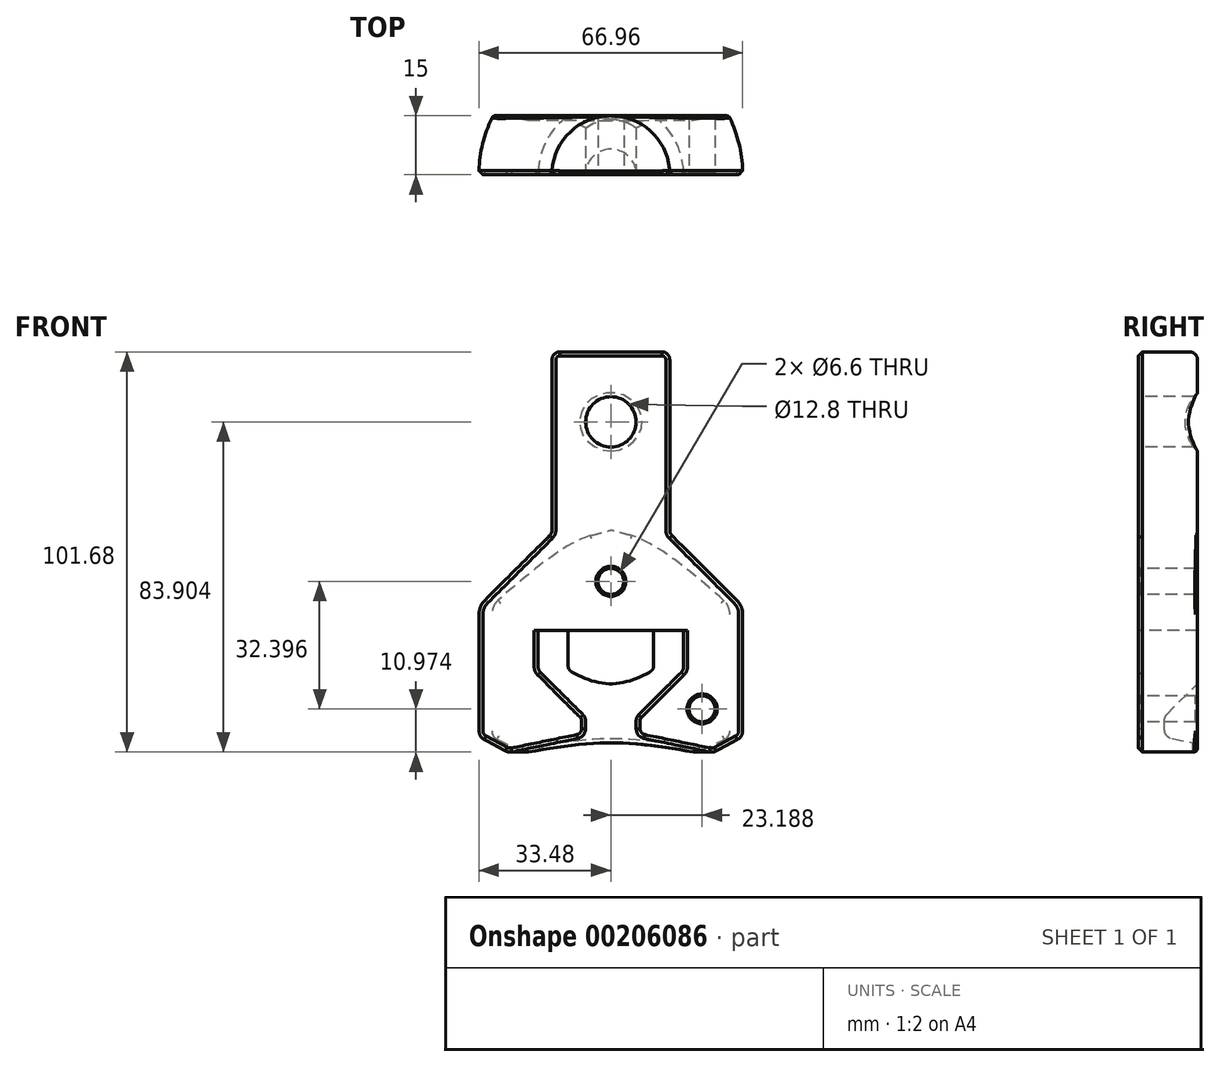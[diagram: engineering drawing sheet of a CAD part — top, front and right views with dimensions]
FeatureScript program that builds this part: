
annotation { "Feature Type Name" : "Feature", "Feature Type Description" : "" }
export const myFeature = defineFeature(function(context is Context, id is Id, definition is map)
    precondition{}
    {
        {
            var Q0;
            Q0=qCreatedBy(makeId("Front.planeOp"),FACE);
            var sketch = newSketch(context, id + "F0", { "sketchPlane" : qUnion([Q0])});
            skLineSegment(sketch, "E0", {"start": v(6.5, 0) * mm, "end": v(18.5, 12) * mm});
            skLineSegment(sketch, "E1", {"start": v(18.5, 12) * mm, "end": v(18.5, 22) * mm});
            skLineSegment(sketch, "E2", {"start": v(18.5, 22) * mm, "end": v(0, 22) * mm});
            skLineSegment(sketch, "E3", {"start": v(6.5, 0) * mm, "end": v(33.5, 0) * mm});
            skLineSegment(sketch, "E4", {"start": v(33.5, 0) * mm, "end": v(33.5, 28.21) * mm});
            skLineSegment(sketch, "E5", {"start": v(15, 92.81) * mm, "end": v(0, 92.81) * mm});
            skLineSegment(sketch, "E6", {"start": v(0, 92.81) * mm, "end": v(0, 22) * mm});
            skCircle(sketch, "E7", {"center": v(0, 75.03) * mm, "radius": 6.35 * mm});
            skPoint(sketch, "E8", {"position": v(0, 81.38) * mm});
            skLineSegment(sketch, "E9.bottom", {"start": v(18.5, 22) * mm, "end": v(-18.5, 22) * mm});
            skLineSegment(sketch, "E9.top", {"start": v(18.5, 0) * mm, "end": v(-18.5, 0) * mm});
            skLineSegment(sketch, "E9.left", {"start": v(18.5, 22) * mm, "end": v(18.5, 0) * mm});
            skLineSegment(sketch, "E9.right", {"start": v(-18.5, 22) * mm, "end": v(-18.5, 0) * mm});
            skLineSegment(sketch, "E10", {"start": v(15, 92.81) * mm, "end": v(15, 46.71) * mm});
            skLineSegment(sketch, "E11", {"start": v(15, 46.71) * mm, "end": v(33.5, 28.21) * mm});
            skLineSegment(sketch, "E12", {"start": v(6.5, 0) * mm, "end": v(6.5, -5) * mm});
            skLineSegment(sketch, "E13", {"start": v(6.5, -5) * mm, "end": v(33.5, -5) * mm});
            skLineSegment(sketch, "E14", {"start": v(33.5, -5) * mm, "end": v(33.5, 0) * mm});
            skLineSegment(sketch, "E15", {"start": v(6.5, -5) * mm, "end": v(26, -9) * mm});
            skLineSegment(sketch, "E16", {"start": v(26, -9) * mm, "end": v(33.5, -5) * mm});
            skLineSegment(sketch, "E17", {"start": v(18.5, 22) * mm, "end": v(29.1, 32.6) * mm, "construction": true});
            skSolve(sketch);
        }
        {
            var Q0;
            {var subQ0=sQuery(id+"F0.wireOp",EDGE,"E7");var subQ1=sQuery(id+"F0.wireOp",EDGE,"E6");var subQ2=makeQuery(id+"F0.imprint","INTERSECT",VERTEX,{"disambiguationData":[OD(0.0)],"derivedFrom":[subQ1,subQ0]});Q0=makeQuery(id+"F0.imprint","IMPRINT",FACE,{"disambiguationData":[TD([[makeQuery(id+"F0.imprint","IMPRINT",EDGE,{"disambiguationData":[TD([[subQ2,-1.0]])],"derivedFrom":subQ1}),1.0]])]});}
            var Q1;
            {var subQ10=sQuery(id+"F0.wireOp",EDGE,"E3");Q1=makeQuery(id+"F0.imprint","IMPRINT",FACE,{"disambiguationData":[TD([[makeQuery(id+"F0.imprint","IMPRINT",EDGE,{"derivedFrom":subQ10}),1.0]])]});}
            var Q2;
            {var subQ0=sQuery(id+"F0.wireOp",EDGE,"E0");Q2=makeQuery(id+"F0.imprint","IMPRINT",FACE,{"disambiguationData":[TD([[makeQuery(id+"F0.imprint","IMPRINT",EDGE,{"derivedFrom":subQ0}),-1.0]])]});}
            var Q3;
            {var subQ2=sQuery(id+"F0.wireOp",EDGE,"E3");Q3=makeQuery(id+"F0.imprint","IMPRINT",FACE,{"disambiguationData":[TD([[makeQuery(id+"F0.imprint","IMPRINT",EDGE,{"derivedFrom":subQ2}),-1.0]])]});}
            var Q4;
            Q4=makeQuery(id+"F0.imprint","IMPRINT",FACE,{"disambiguationData":[TD([[makeQuery(id+"F0.imprint","IMPRINT",EDGE,{"derivedFrom":sQuery(id+"F0.wireOp",EDGE,"E13")}),-1.0]])]});
            var Q5;
            Q5=sQuery(id+"F0.wireOp",EDGE,"E6");
            revolve(context, id + "F1", {"entities" : qUnion([Q0, Q1, Q2, Q3, Q4]), "axis" : qUnion([Q5]), "revolveType" : RevolveType.ONE_DIRECTION, "oppositeDirection" : true, "angle" : 180 * degree});
        }
        {
            var Q0;
            Q0=makeQuery(id+"F1.opRevolve","SWEPT_EDGE",EDGE,{"disambiguationData":[OSD([sQuery(id+"F0.wireOp",EDGE,"FI2kWnsq-bYjR-toCD-jMWB-uaBhb8gfH4dN"),sQuery(id+"F0.wireOp",EDGE,"DZJPYPuS-xWPI-OwPd-xfq3-0R899iDrHJfV")])]});
            var Q1;
            Q1=makeQuery(id+"F1.opRevolve","SWEPT_EDGE",EDGE,{"disambiguationData":[OSD([sQuery(id+"F0.wireOp",EDGE,"DZJPYPuS-xWPI-OwPd-xfq3-0R899iDrHJfV"),sQuery(id+"F0.wireOp",EDGE,"E5")])]});
            var Q2;
            Q2=makeQuery(id+"F1.opRevolve","SWEPT_EDGE",EDGE,{"disambiguationData":[OSD([sQuery(id+"F0.wireOp",EDGE,"E0"),sQuery(id+"F0.wireOp",EDGE,"E9.top")])]});
            var Q3;
            Q3=makeQuery(id+"F1.opRevolve","SWEPT_EDGE",EDGE,{"disambiguationData":[OSD([sQuery(id+"F0.wireOp",EDGE,"E0"),sQuery(id+"F0.wireOp",EDGE,"E9.left")])]});
            var Q4;
            Q4=makeQuery(id+"F1.opRevolve","SWEPT_EDGE",EDGE,{"disambiguationData":[OSD([sQuery(id+"F0.wireOp",EDGE,"E10"),sQuery(id+"F0.wireOp",EDGE,"E11")])]});
            fillet(context, id + "F2", {"entities" : qUnion([Q0, Q1, Q2, Q3, Q4]), "radius" : 2 * mm, "tangentPropagation" : true, "allowEdgeOverflow" : false});
        }
        {
            var Q0;
            Q0=qCreatedBy(makeId("Front.planeOp"),FACE);
            var sketch = newSketch(context, id + "F3", { "sketchPlane" : qUnion([Q0])});
            skCircle(sketch, "E18", {"center": v(0, 75.03) * mm, "radius": 6.4 * mm});
            skCircle(sketch, "E19", {"center": v(23.19, 2.1) * mm, "radius": 4.1 * mm, "construction": true});
            skCircle(sketch, "E20", {"center": v(23.19, 2.1) * mm, "radius": 3.3 * mm});
            skCircle(sketch, "E21", {"center": v(23.19, 2.1) * mm, "radius": 7.5 * mm});
            skLineSegment(sketch, "E22", {"start": v(23.19, 2.1) * mm, "end": v(33.5, 2.1) * mm, "construction": true});
            skLineSegment(sketch, "E23", {"start": v(23.19, 2.1) * mm, "end": v(15.9, 9.4) * mm, "construction": true});
            skLineSegment(sketch, "E24", {"start": v(23.19, 2.1) * mm, "end": v(21.12, -8) * mm, "construction": true});
            skLineSegment(sketch, "E25", {"start": v(23.19, 9.6) * mm, "end": v(33.5, 9.6) * mm});
            skCircle(sketch, "E26", {"center": v(23.19, 2.1) * mm, "radius": 6 * mm, "construction": true});
            skLineSegment(sketch, "E27", {"start": v(23.19, -5.4) * mm, "end": v(32.76, -5.4) * mm});
            skLineSegment(sketch, "E28", {"start": v(32.76, -5.4) * mm, "end": v(33.5, -5.4) * mm});
            skLineSegment(sketch, "E29", {"start": v(33.5, -5.4) * mm, "end": v(33.5, 9.6) * mm});
            skCircle(sketch, "E30", {"center": v(0, 34.5) * mm, "radius": 3.3 * mm});
            skCircle(sketch, "E31", {"center": v(0, 34.5) * mm, "radius": 7.5 * mm});
            skSolve(sketch);
        }
        {
            var Q0;
            Q0=makeQuery(id+"F3.imprint","IMPRINT",FACE,{"disambiguationData":[TD([[makeQuery(id+"F3.imprint","IMPRINT",EDGE,{"derivedFrom":sQuery(id+"F3.wireOp",EDGE,"E18")}),1.0]])]});
            extrude(context, id + "F4", {"entities" : qUnion([Q0]), "operationType" : NewBodyOperationType.REMOVE, "endBound" : BoundingType.THROUGH_ALL, "oppositeDirection" : true, "depth" : 25 * mm});
        }
        {
            var Q0;
            Q0=makeQuery(id+"F1.opRevolve","SWEPT_EDGE",EDGE,{"disambiguationData":[OSD([sQuery(id+"F0.wireOp",EDGE,"E4"),sQuery(id+"F0.wireOp",EDGE,"FI2kWnsq-bYjR-toCD-jMWB-uaBhb8gfH4dN")])]});
            var Q1;
            Q1=makeQuery(id+"F1.opRevolve","SWEPT_EDGE",EDGE,{"disambiguationData":[OSD([sQuery(id+"F0.wireOp",EDGE,"E3"),sQuery(id+"F0.wireOp",EDGE,"E4")])]});
            fillet(context, id + "F5", {"entities" : qUnion([Q0, Q1]), "radius" : 5 * mm, "tangentPropagation" : true, "allowEdgeOverflow" : false});
        }
        {
            var Q0;
            Q0=makeQuery(id+"F3.imprint","IMPRINT",FACE,{"disambiguationData":[TD([[makeQuery(id+"F3.imprint","IMPRINT",EDGE,{"derivedFrom":sQuery(id+"F3.wireOp",EDGE,"5mAL5B5x-17wX-fpjQ-DvXL-zQjTYSrSRtwO")}),1.0]])]});
            var Q1;
            Q1=makeQuery(id+"F3.imprint","IMPRINT",FACE,{"disambiguationData":[TD([[makeQuery(id+"F3.imprint","IMPRINT",EDGE,{"derivedFrom":sQuery(id+"F3.wireOp",EDGE,"E20")}),1.0]])]});
            var Q2;
            Q2=makeQuery(id+"F3.imprint","IMPRINT",FACE,{"disambiguationData":[TD([[makeQuery(id+"F3.imprint","IMPRINT",EDGE,{"derivedFrom":sQuery(id+"F3.wireOp",EDGE,"E20")}),-1.0]])]});
            var Q3;
            Q3=makeQuery(id+"F3.imprint","IMPRINT",FACE,{"disambiguationData":[TD([[makeQuery(id+"F3.imprint","IMPRINT",EDGE,{"derivedFrom":sQuery(id+"F3.wireOp",EDGE,"5mAL5B5x-17wX-fpjQ-DvXL-zQjTYSrSRtwO")}),-1.0]])]});
            var Q4;
            {var subQ0=sQuery(id+"F3.wireOp",EDGE,"QcyNRo9u-gzep-EV6m-rlQG-XWZFFJgr7ENr");Q4=makeQuery(id+"F3.imprint","IMPRINT",FACE,{"disambiguationData":[TD([[makeQuery(id+"F3.imprint","IMPRINT",EDGE,{"derivedFrom":subQ0}),-1.0]])]});}
            var Q5;
            {var subQ0=sQuery(id+"F3.wireOp",EDGE,"wycjBb6X-auFu-LVRJ-BCHS-l95IwHfiS5XZ");Q5=makeQuery(id+"F3.imprint","IMPRINT",FACE,{"disambiguationData":[TD([[makeQuery(id+"F3.imprint","IMPRINT",EDGE,{"derivedFrom":subQ0}),1.0]])]});}
            var Q6;
            {var subQ1=sQuery(id+"F3.wireOp",EDGE,"g40P36om-zgSY-dNlI-F9Me-a3eTcjUbRJQn");Q6=makeQuery(id+"F3.imprint","IMPRINT",FACE,{"disambiguationData":[TD([[makeQuery(id+"F3.imprint","IMPRINT",EDGE,{"derivedFrom":subQ1}),-1.0]])]});}
            var Q7;
            {var subQ1=sQuery(id+"F3.wireOp",EDGE,"E25");Q7=makeQuery(id+"F3.imprint","IMPRINT",FACE,{"disambiguationData":[TD([[makeQuery(id+"F3.imprint","IMPRINT",EDGE,{"derivedFrom":subQ1}),-1.0]])]});}
            var Q8;
            Q8=makeQuery(id+"F3.imprint","IMPRINT",FACE,{"disambiguationData":[TD([[makeQuery(id+"F3.imprint","IMPRINT",EDGE,{"derivedFrom":sQuery(id+"F3.wireOp",EDGE,"E30")}),-1.0]])]});
            var Q9;
            Q9=makeQuery(id+"F3.imprint","IMPRINT",FACE,{"disambiguationData":[TD([[makeQuery(id+"F3.imprint","IMPRINT",EDGE,{"derivedFrom":sQuery(id+"F3.wireOp",EDGE,"E30")}),1.0]])]});
            extrude(context, id + "F6", {"entities" : qUnion([Q0, Q1, Q2, Q3, Q4, Q5, Q6, Q7, Q8, Q9]), "operationType" : NewBodyOperationType.REMOVE, "endBound" : BoundingType.THROUGH_ALL, "oppositeDirection" : true, "depth" : 25 * mm, "hasSecondDirection" : true, "secondDirectionOppositeDirection" : true, "secondDirectionDepth" : 15 * mm});
        }
        {
            var Q0;
            Q0=makeQuery(id+"F3.imprint","IMPRINT",FACE,{"disambiguationData":[TD([[makeQuery(id+"F3.imprint","IMPRINT",EDGE,{"derivedFrom":sQuery(id+"F3.wireOp",EDGE,"E20")}),1.0]])]});
            var Q1;
            Q1=makeQuery(id+"F3.imprint","IMPRINT",FACE,{"disambiguationData":[TD([[makeQuery(id+"F3.imprint","IMPRINT",EDGE,{"derivedFrom":sQuery(id+"F3.wireOp",EDGE,"5mAL5B5x-17wX-fpjQ-DvXL-zQjTYSrSRtwO")}),1.0]])]});
            var Q2;
            Q2=makeQuery(id+"F3.imprint","IMPRINT",FACE,{"disambiguationData":[TD([[makeQuery(id+"F3.imprint","IMPRINT",EDGE,{"derivedFrom":sQuery(id+"F3.wireOp",EDGE,"E30")}),1.0]])]});
            extrude(context, id + "F7", {"entities" : qUnion([Q0, Q1, Q2]), "operationType" : NewBodyOperationType.REMOVE, "endBound" : BoundingType.THROUGH_ALL, "oppositeDirection" : true, "depth" : 25 * mm});
        }
        {
            var Q0;
            Q0=makeQuery(id+"F1.opRevolve","SWEPT_EDGE",EDGE,{"disambiguationData":[OSD([sQuery(id+"F0.wireOp",EDGE,"E9.bottom"),sQuery(id+"F0.wireOp",EDGE,"E9.left")])]});
            var Q1;
            Q1=makeQuery(id+"F6.boolean.opBoolean","COPY",EDGE,{"derivedFrom":makeQuery(id+"F6.opExtrude","CAP_EDGE",EDGE,{"disambiguationData":[OSD([sQuery(id+"F3.wireOp",EDGE,"9wDBNp5m-kJux-o5BL-9qMn-IMAsFSHTvKGn")])],"isStart":true})});
            var Q2;
            Q2=makeQuery(id+"F6.boolean.opBoolean","COPY",EDGE,{"derivedFrom":makeQuery(id+"F6.opExtrude","SWEPT_EDGE",EDGE,{"disambiguationData":[OSD([sQuery(id+"F3.wireOp",EDGE,"mV04Bt11-Ou6Z-f7Wr-9GvA-9ZIzNDh8KCzS"),sQuery(id+"F3.wireOp",EDGE,"9wDBNp5m-kJux-o5BL-9qMn-IMAsFSHTvKGn")])]})});
            var Q3;
            Q3=makeQuery(id+"Fr8qs1tSwam8Usj_1.1.F6.boolean.opBoolean","COPY",EDGE,{"derivedFrom":makeQuery(id+"Fr8qs1tSwam8Usj_1.1.F6.opExtrude","CAP_EDGE",EDGE,{"disambiguationData":[OSD([sQuery(id+"F3.wireOp",EDGE,"9wDBNp5m-kJux-o5BL-9qMn-IMAsFSHTvKGn")])],"isStart":true})});
            var Q4;
            Q4=makeQuery(id+"F1.opRevolve","SWEPT_EDGE",EDGE,{"disambiguationData":[OSD([sQuery(id+"F0.wireOp",EDGE,"E12"),sQuery(id+"F0.wireOp",EDGE,"E13")])]});
            var Q5;
            Q5=makeQuery(id+"F1.opRevolve","SWEPT_EDGE",EDGE,{"disambiguationData":[OSD([sQuery(id+"F0.wireOp",EDGE,"E15"),sQuery(id+"F0.wireOp",EDGE,"E16")])]});
            var Q6;
            {var subQ0=sQuery(id+"F0.wireOp",EDGE,"E14");var subQ1=sQuery(id+"F0.wireOp",EDGE,"E16");var subQ2=sQuery(id+"F3.wireOp",EDGE,"E21");Q6=makeQuery(id+"Fr8qs1tSwam8Usj_1.1.F6.boolean.opBoolean","SPLIT",EDGE,{"disambiguationData":[TD([makeQuery(id+"F6.boolean.opBoolean","COPY",FACE,{"derivedFrom":makeQuery(id+"F6.opExtrude","SWEPT_FACE",FACE,{"disambiguationData":[OSD([subQ2])]})})])],"derivedFrom":makeQuery(id+"F6.boolean.opBoolean","SPLIT",EDGE,{"disambiguationData":[OD(1.0)],"derivedFrom":makeQuery(id+"F1.opRevolve","SWEPT_EDGE",EDGE,{"disambiguationData":[OSD([sQuery(id+"F0.wireOp",EDGE,"E13"),subQ0,subQ1])]})})});}
            fillet(context, id + "F8", {"entities" : qUnion([Q0, Q1, Q2, Q3, Q4, Q5, Q6]), "radius" : 2.5 * mm, "tangentPropagation" : true, "allowEdgeOverflow" : false});
        }
        {
            var Q0;
            Q0=qCreatedBy(makeId("Right.planeOp"),FACE);
            var sketch = newSketch(context, id + "F9", { "sketchPlane" : qUnion([Q0])});
            skLineSegment(sketch, "E32.bottom", {"start": v(15, 92.81) * mm, "end": v(33.5, 92.81) * mm});
            skLineSegment(sketch, "E32.left", {"start": v(15, 92.81) * mm, "end": v(15, -18.82) * mm});
            skLineSegment(sketch, "E32.right", {"start": v(33.5, 92.81) * mm, "end": v(33.5, -18.82) * mm});
            skLineSegment(sketch, "E33", {"start": v(15, -18.82) * mm, "end": v(33.5, -18.82) * mm});
            skSolve(sketch);
        }
        {
            var Q0;
            Q0 = qSketchRegion(id + "F9", true);
            extrude(context, id + "F10", {"entities" : qUnion([Q0]), "operationType" : NewBodyOperationType.REMOVE, "endBound" : BoundingType.THROUGH_ALL, "depth" : 25 * mm, "hasSecondDirection" : true, "secondDirectionBound" : SecondDirectionBoundingType.THROUGH_ALL, "secondDirectionOppositeDirection" : true, "secondDirectionDepth" : 25 * mm});
        }
        {
            var Q0;
            Q0=makeQuery(id+"F4.boolean.opBoolean","INTERSECT",EDGE,{"derivedFrom":[makeQuery(id+"F1.opRevolve","SWEPT_FACE",FACE,{"disambiguationData":[OSD([sQuery(id+"F0.wireOp",EDGE,"E10")])]}),makeQuery(id+"F4.opExtrude","SWEPT_FACE",FACE,{"disambiguationData":[OSD([sQuery(id+"F3.wireOp",EDGE,"E18")])]})]});
            var Q1;
            Q1=makeQuery(id+"F4.boolean.opBoolean","COPY",EDGE,{"derivedFrom":makeQuery(id+"F4.opExtrude","CAP_EDGE",EDGE,{"disambiguationData":[OSD([sQuery(id+"F3.wireOp",EDGE,"E18")])],"isStart":true})});
            var Q2;
            Q2=makeQuery(id+"F1.opRevolve","CAP_EDGE",EDGE,{"disambiguationData":[OSD([sQuery(id+"F0.wireOp",EDGE,"E10")])],"isStart":true});
            chamfer(context, id + "F11", {"entities" : qUnion([Q0, Q1, Q2]), "width" : 1 * mm, "tangentPropagation" : true});
        }
        {
            var Q0;
            Q0=makeQuery(id+"F10.boolean.opBoolean","INTERSECT",EDGE,{"derivedFrom":[makeQuery(id+"F1.opRevolve","SWEPT_FACE",FACE,{"disambiguationData":[OSD([sQuery(id+"F0.wireOp",EDGE,"E11")])]}),makeQuery(id+"F10.opExtrude","SWEPT_FACE",FACE,{"disambiguationData":[OSD([sQuery(id+"F9.wireOp",EDGE,"E32.left")])]})]});
            var Q1;
            Q1=makeQuery(id+"F10.boolean.opBoolean","INTERSECT",EDGE,{"derivedFrom":[makeQuery(id+"F6.boolean.opBoolean","COPY",FACE,{"derivedFrom":makeQuery(id+"F6.opExtrude","SWEPT_FACE",FACE,{"disambiguationData":[OSD([sQuery(id+"F3.wireOp",EDGE,"E21")])]})}),makeQuery(id+"F10.opExtrude","SWEPT_FACE",FACE,{"disambiguationData":[OSD([sQuery(id+"F9.wireOp",EDGE,"E32.left")])]})]});
            var Q2;
            Q2=makeQuery(id+"F10.boolean.opBoolean","INTERSECT",EDGE,{"derivedFrom":[makeQuery(id+"Fr8qs1tSwam8Usj_1.1.F6.boolean.opBoolean","COPY",FACE,{"derivedFrom":makeQuery(id+"Fr8qs1tSwam8Usj_1.1.F6.opExtrude","SWEPT_FACE",FACE,{"disambiguationData":[OSD([sQuery(id+"F3.wireOp",EDGE,"E21")])]})}),makeQuery(id+"F10.opExtrude","SWEPT_FACE",FACE,{"disambiguationData":[OSD([sQuery(id+"F9.wireOp",EDGE,"E32.left")])]})]});
            fillet(context, id + "F12", {"entities" : qUnion([Q0, Q1, Q2]), "radius" : 1 * mm, "tangentPropagation" : true, "allowEdgeOverflow" : false});
        }
        {
            var Q0;
            Q0=makeQuery(id+"F7.boolean.opBoolean","INTERSECT",EDGE,{"derivedFrom":[makeQuery(id+"F6.boolean.opBoolean","COPY",FACE,{"derivedFrom":makeQuery(id+"F6.opExtrude","CAP_FACE",FACE,{"disambiguationData":[OSD([sQuery(id+"F3.wireOp",EDGE,"E31")])],"isStart":true})}),makeQuery(id+"F7.opExtrude","SWEPT_FACE",FACE,{"disambiguationData":[OSD([sQuery(id+"F3.wireOp",EDGE,"E30")])]})]});
            var Q1;
            Q1=makeQuery(id+"Fr8qs1tSwam8Usj_1.1.F7.boolean.opBoolean","INTERSECT",EDGE,{"derivedFrom":[makeQuery(id+"Fr8qs1tSwam8Usj_1.1.F6.boolean.opBoolean","COPY",FACE,{"derivedFrom":makeQuery(id+"Fr8qs1tSwam8Usj_1.1.F6.opExtrude","CAP_FACE",FACE,{"disambiguationData":[OSD([sQuery(id+"F3.wireOp",EDGE,"E21"),sQuery(id+"F3.wireOp",EDGE,"E25"),sQuery(id+"F3.wireOp",EDGE,"E27"),sQuery(id+"F3.wireOp",EDGE,"E28"),sQuery(id+"F3.wireOp",EDGE,"E29")])],"isStart":true})}),makeQuery(id+"Fr8qs1tSwam8Usj_1.1.F7.opExtrude","SWEPT_FACE",FACE,{"disambiguationData":[OSD([sQuery(id+"F3.wireOp",EDGE,"E20")])]})]});
            var Q2;
            Q2=makeQuery(id+"F7.boolean.opBoolean","INTERSECT",EDGE,{"derivedFrom":[makeQuery(id+"F6.boolean.opBoolean","COPY",FACE,{"derivedFrom":makeQuery(id+"F6.opExtrude","CAP_FACE",FACE,{"disambiguationData":[OSD([sQuery(id+"F3.wireOp",EDGE,"E21"),sQuery(id+"F3.wireOp",EDGE,"E25"),sQuery(id+"F3.wireOp",EDGE,"E27"),sQuery(id+"F3.wireOp",EDGE,"E28"),sQuery(id+"F3.wireOp",EDGE,"E29")])],"isStart":true})}),makeQuery(id+"F7.opExtrude","SWEPT_FACE",FACE,{"disambiguationData":[OSD([sQuery(id+"F3.wireOp",EDGE,"E20")])]})]});
            var Q3;
            Q3=makeQuery(id+"F7.boolean.opBoolean","COPY",FACE,{"derivedFrom":makeQuery(id+"F7.opExtrude","SWEPT_FACE",FACE,{"disambiguationData":[OSD([sQuery(id+"F3.wireOp",EDGE,"E20")])]})});
            var Q4;
            Q4=makeQuery(id+"Fr8qs1tSwam8Usj_1.1.F7.boolean.opBoolean","COPY",FACE,{"derivedFrom":makeQuery(id+"Fr8qs1tSwam8Usj_1.1.F7.opExtrude","SWEPT_FACE",FACE,{"disambiguationData":[OSD([sQuery(id+"F3.wireOp",EDGE,"E20")])]})});
            var Q5;
            Q5=makeQuery(id+"F7.boolean.opBoolean","COPY",FACE,{"derivedFrom":makeQuery(id+"F7.opExtrude","SWEPT_FACE",FACE,{"disambiguationData":[OSD([sQuery(id+"F3.wireOp",EDGE,"E30")])]})});
            chamfer(context, id + "F13", {"entities" : qUnion([Q0, Q1, Q2, Q3, Q4, Q5]), "width" : .5 * mm, "tangentPropagation" : true});
        }
    });
